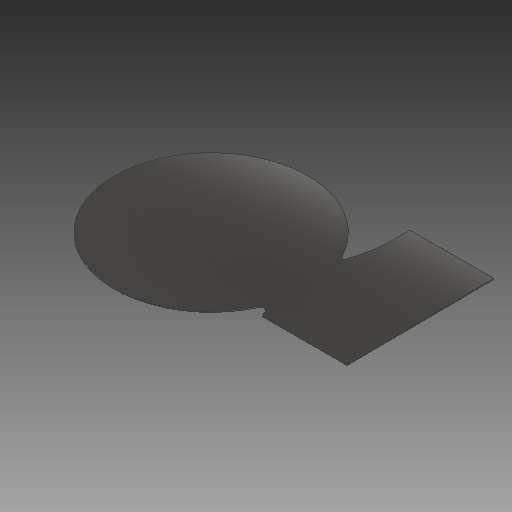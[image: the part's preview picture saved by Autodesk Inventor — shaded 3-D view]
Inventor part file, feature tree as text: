
AUTODESK INVENTOR PART (.ipt)
format: ipt  version: 2018 (Build 220112000, 112)  size: 114,176 bytes
history: native  units: mm
features: other x3, sketch x1
ambient origin geometry x8: Origin, YZ Plane, XZ Plane, XY Plane, X Axis, Y Axis, Z Axis, Center Point
bodies: Volumenkörper1 (feature_tree)
feature tree (4):
  other  "Solarpanel_MIR2.ipt"
  other  "Volumenkörper1::Solarpanel_MIR2.ipt"
  other  "Bezeichnung1"
  sketch  "Skizze6"  dims[d0=10.0mm]
